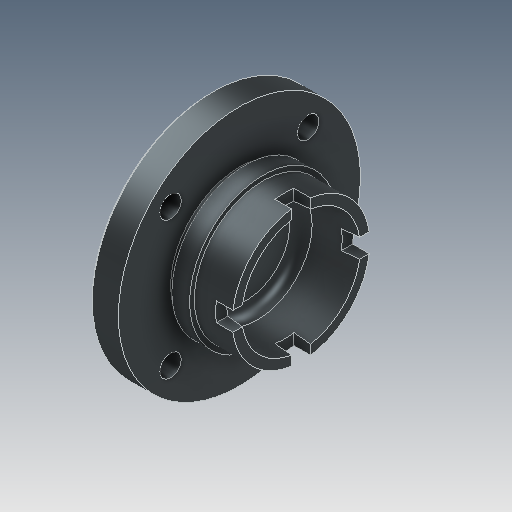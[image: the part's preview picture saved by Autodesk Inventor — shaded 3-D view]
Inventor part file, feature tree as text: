
AUTODESK INVENTOR PART (.ipt)
format: ipt  version: 2025 (Build 290162000, 162)  size: 225,792 bytes
history: native  units: in
note: dims shown in document units (in); Inventor stores cm internally (conversion verified against a paired STEP export)
features: sketch x5, extrude x3, revolve x1, chamfer x1, fillet x1
ambient origin geometry x8: Origin, YZ Plane, XZ Plane, XY Plane, X Axis, Y Axis, Z Axis, Center Point
bodies: 实体1 (feature_tree)
feature tree (11):
  revolve  "旋转1"  [1 undecoded]
  extrude  "拉伸1"  Depth=0.4724in
  extrude  "拉伸2"  Depth=1.1417in
  extrude  "拉伸3"  Depth=0.3937in
  chamfer  "倒角1"  Angle=45.0deg  [1 undecoded]
  fillet  "圆角1"  Radius=0.0394in
  sketch  "草图1"  dims[d3=0.315in d0=0.3543in d1=1.0236in d2=2.0079in]
  sketch  "草图2"  dims[d6=1.2205in d7=1.1417in]
  sketch  "草图3"  dims[d8=0.3937in d9=0.0984in]
  sketch  "草图4"  dims[d10=1.1417in d11=45.0deg d12=0.0394in d13=0.5906in d14=0.9843in d15=0.5792in d16=90.0deg d17=0.2756in d18=0.315in d19=0.0in d20=0.2756in d21=0.315in d22=0.0in d23=0.3543in d24=1.6142in d25=1.5748in d27=360.0deg d29=0.315in d30=0.0in d31=0.0394in d32=0.0787in d33=45.0deg d34=0.1969in d35=45.0deg]
  sketch  "草图 - 环形阵列1"  dims[d4=1.0236in d5=0.4724in]
note: 2 required parameter values undecoded (feature->parameter linkage not recoverable at this tier; creation-order binding heuristic only, values carry confidence <= 0.55)